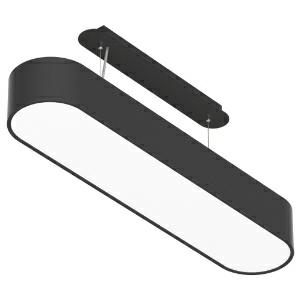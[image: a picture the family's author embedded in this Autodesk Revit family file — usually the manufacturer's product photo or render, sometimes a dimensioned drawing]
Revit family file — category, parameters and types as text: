
# Revit family: smoothline_930x200_hl_led_29w_2240lm_3000k_cri80_410-1430
name_source: partatom
category: Leuchten
revit_build: Autodesk Revit 2016 (Build: 20190508_0715(x64)
units: mm (PartAtom-declared; Revit-internal decimal feet)

## family parameters
Basisbauteil = Fläche
Beim Laden mit Abzugskörper schneiden = Nein
Bemaßung runder Anschluss = Durchmesser verwenden
Gemeinsam genutzt = Nein
Lichtquelle = Nein
Raumberechnungspunkt = Nein
Teiletyp = Normal

## types (1)
- 410-1430-D01 (9 x LED, 429 lm, 3.2 W, 3000K)
    Approval mark = CE
    Beschreibung = The pendant luminaire SMOOTHLINE from the familiy SMOOTHY consists of aluminum-extruded profile. Charming SOFT-EDGE design ensure unparalleled styling. The ballast is integrated and allows for an operation with 220-240V (50/60Hz). SMOOTHLINE (# 410-1430) ist not dimmable (on/off). The luminaire with direct illumination and corresponds to protection class SK1 at IP20.
    CIE Flux Codes = 47 78 95 100 57
    Color Rendering = 1B/80…89
    Color Temperature = 3000K
    Height = 120 mm
    Hersteller = Prolicht
    Lamp Light Flux = 429 lm
    Lamp Power = 3.2 W
    Lamp count = 9
    Lampe = 9 x LED
    Length = 930 mm
    Luminous efficacy = 76 lm/W
    ModVariant = Nein
    Modell = 410-1430
    Mounting Place = Ceiling
    Mounting Type = Pendant
    Number of Poles = 1
    OnlyDefault = Ja
    Power Factor = 1
    Product Name = SMOOTHLINE 930x200 HL LED 29W 2240lm 3000K CRI80
    Product group = Suspended lights
    ProductGroupID = 941
    Protection Class = Protection class I
    Protection Degree = IP 20
    RLX_Detail_Level = 1
    RlxData = <blob elided: 43005 chars, md5=5a3130e7>
    Scheinlast = 29 VA
    Socket = socket
    Standby Power = 0 W
    System Light Flux = 2191 lm
    System Power = 29 W
    Typenbild = 410-1430.jpg
    URL = http://relux.com
    VarID = 410-1430-d01
    Voltage = 0 V
    Vorgabe-Ansicht = 1800 mm
    Weight = 0.00 kg
    Width = 200 mm  [stored 0.656168 ft]

note: [stored X ft] marks values corroborated as IEEE doubles in the binary element streams (Revit-internal decimal feet)

## geometry (parser evidence)
native form markers: Sweep x14
no freeform markers — native parametric forms only
